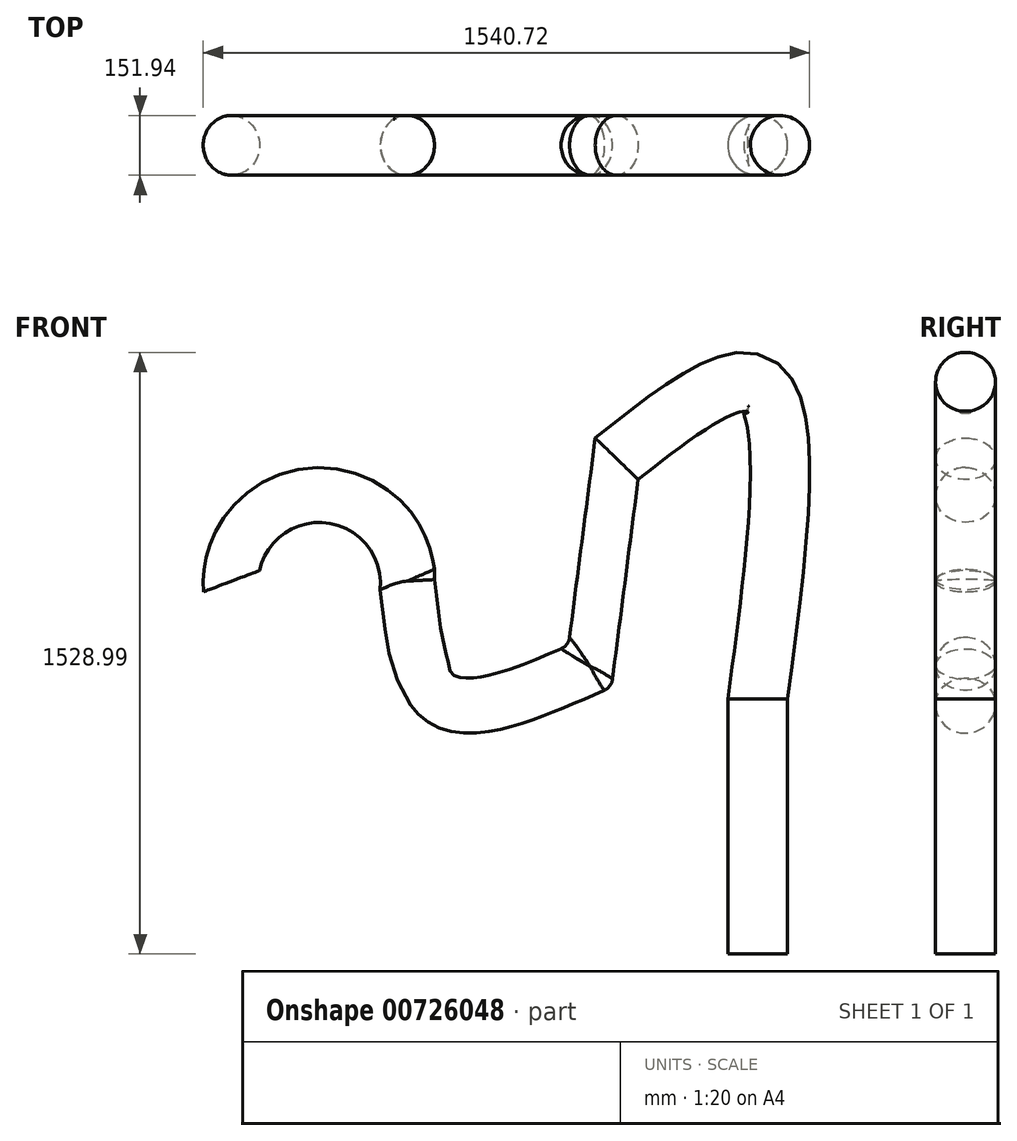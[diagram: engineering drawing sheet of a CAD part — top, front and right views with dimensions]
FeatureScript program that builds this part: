
annotation { "Feature Type Name" : "Feature", "Feature Type Description" : "" }
export const myFeature = defineFeature(function(context is Context, id is Id, definition is map)
    precondition{}
    {
        {
            var Q0;
            Q0=qCreatedBy(makeId("Top.planeOp"),FACE);
            var sketch = newSketch(context, id + "F0", { "sketchPlane" : qUnion([Q0])});
            skCircle(sketch, "E0", {"center": v(0, 0) * mm, "radius": 75.97 * mm});
            skSolve(sketch);
        }
        {
            var Q0;
            Q0=qCreatedBy(makeId("Front.planeOp"),FACE);
            var sketch = newSketch(context, id + "F1", { "sketchPlane" : qUnion([Q0])});
            skFitSpline(sketch, "E1", {"points": [v(0, 0) * mm, v(0, 796.62) * mm, v(-358.33, 610.75) * mm], "startDerivative": vector(251.69, 1892.55) * mm, "endDerivative": vector(-1040.87, -823.44) * mm});
            skFitSpline(sketch, "E2", {"points": [v(-358.33, 610.75) * mm, v(-426.24, 83.53) * mm], "startDerivative": vector(-67.91, -527.22) * mm, "endDerivative": vector(-67.91, -527.22) * mm});
            skFitSpline(sketch, "E3", {"points": [v(-426.24, 83.53) * mm, v(-792.62, 0) * mm, v(-890.91, 299.78) * mm], "startDerivative": vector(-831.62, -365.41) * mm, "endDerivative": vector(-86.87, 815.1) * mm});
            skArc(sketch, "E4", {"start": v(-890.91, 299.78) * mm, "mid": v(-1113.94, 516.83) * mm, "end": v(-1336.97, 299.78) * mm});
            skArc(sketch, "E5.filletArc", {"start": v(-432.81, 80.64) * mm, "mid": v(-427.75, 84.66) * mm, "end": v(-425.32, 90.65) * mm});
            skArc(sketch, "E6.filletArc", {"start": v(-354.27, 613.96) * mm, "mid": v(-357.45, 610.25) * mm, "end": v(-358.99, 605.62) * mm});
            skSolve(sketch);
        }
        {
            var Q0;
            Q0=makeQuery(id+"F0.imprint","IMPRINT",FACE,{"disambiguationData":[TD([[makeQuery(id+"F0.imprint","IMPRINT",EDGE,{"derivedFrom":sQuery(id+"F0.wireOp",EDGE,"E0")}),1.0]])]});
            var Q1;
            Q1=sQuery(id+"F1.wireOp",EDGE,"E1");
            sweep(context, id + "F2", {"profiles" : qUnion([Q0]), "path" : qUnion([Q1])});
        }
        {
            var Q0;
            Q0=makeQuery(id+"F2.opSweep","CAP_FACE",FACE,{"disambiguationData":[OSD([sQuery(id+"F0.wireOp",EDGE,"E0"),sQuery(id+"F1.wireOp",VERTEX,"E1.end")])],"isStart":false});
            var Q1;
            Q1=sQuery(id+"F1.wireOp",EDGE,"E2");
            sweep(context, id + "F3", {"operationType" : NewBodyOperationType.ADD, "profiles" : qUnion([Q0]), "path" : qUnion([Q1])});
        }
        {
            var Q0;
            Q0=makeQuery(id+"F3.opSweep","CAP_FACE",FACE,{"disambiguationData":[OSD([sQuery(id+"F0.wireOp",EDGE,"E0"),sQuery(id+"F1.wireOp",VERTEX,"E1.end"),sQuery(id+"F1.wireOp",VERTEX,"E2.end")])],"isStart":false});
            var Q1;
            Q1=sQuery(id+"F1.wireOp",EDGE,"E3");
            var Q2;
            Q2=sQuery(id+"F1.wireOp",EDGE,"E4");
            sweep(context, id + "F4", {"operationType" : NewBodyOperationType.ADD, "profiles" : qUnion([Q0]), "path" : qUnion([Q1, Q2])});
        }
        {
            var Q0;
            {var subQ0=sQuery(id+"F1.wireOp",VERTEX,"E2.end");var subQ1=sQuery(id+"F1.wireOp",VERTEX,"E1.end");var subQ2=sQuery(id+"F0.wireOp",EDGE,"E0");Q0=makeQuery(id+"F4.boolean.opBoolean","MERGE",EDGE,{"derivedFrom":[makeQuery(id+"F3.opSweep","CAP_EDGE",EDGE,{"disambiguationData":[OSD([subQ2,subQ1,subQ0])],"isStart":false}),makeQuery(id+"F4.opSweep","CAP_EDGE",EDGE,{"disambiguationData":[OSD([subQ2,subQ1,subQ0,sQuery(id+"F1.wireOp",VERTEX,"E3.start")])],"isStart":true})]});}
            fillet(context, id + "F5", {"entities" : qUnion([Q0]), "radius" : 36 * mm, "tangentPropagation" : true, "allowEdgeOverflow" : false});
        }
        {
            var Q0;
            Q0=makeQuery(id+"F2.opSweep","CAP_FACE",FACE,{"disambiguationData":[OSD([sQuery(id+"F0.wireOp",EDGE,"E0"),sQuery(id+"F1.wireOp",VERTEX,"E1.start")])],"isStart":true});
            extrude(context, id + "F6", {"entities" : qUnion([Q0]), "operationType" : NewBodyOperationType.ADD, "depth" : 647.7 * mm, "offsetDistance" : 25.4 * mm});
        }
    });
